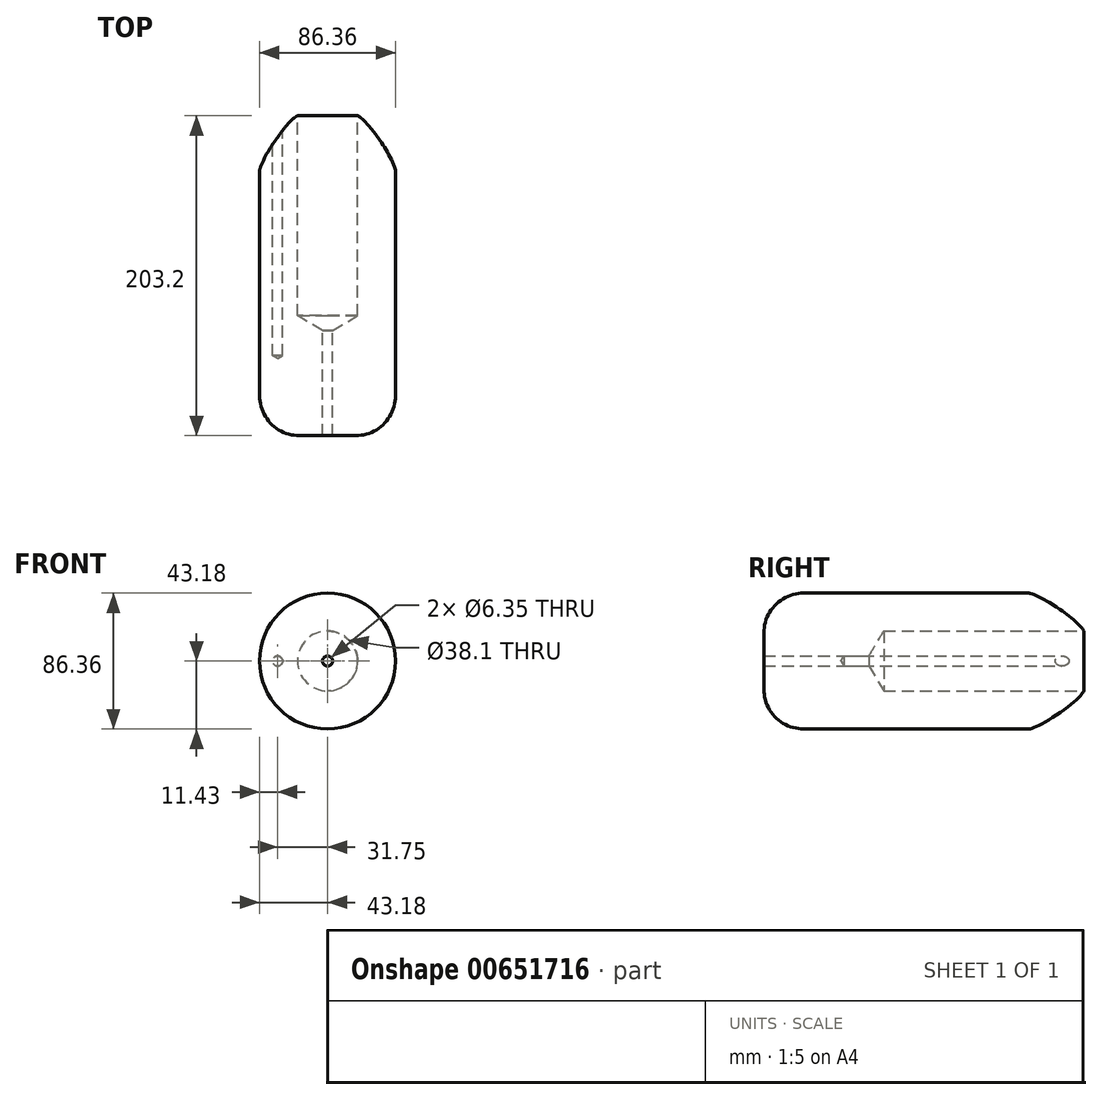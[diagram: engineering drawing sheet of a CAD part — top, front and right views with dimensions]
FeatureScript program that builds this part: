
annotation { "Feature Type Name" : "Feature", "Feature Type Description" : "" }
export const myFeature = defineFeature(function(context is Context, id is Id, definition is map)
    precondition{}
    {
        {
            var Q0;
            Q0=qCreatedBy(makeId("Front.planeOp"),FACE);
            var sketch = newSketch(context, id + "F0", { "sketchPlane" : qUnion([Q0])});
            skCircle(sketch, "E0", {"center": v(0, 0) * mm, "radius": 43.18 * mm});
            skSolve(sketch);
        }
        {
            var Q0;
            Q0=qCreatedBy(makeId("Front.planeOp"),FACE);
            var sketch = newSketch(context, id + "F1", { "sketchPlane" : qUnion([Q0])});
            skCircle(sketch, "E1", {"center": v(0, 0) * mm, "radius": 19.05 * mm});
            skSolve(sketch);
        }
        {
            var Q0;
            Q0=qCreatedBy(makeId("Front.planeOp"),FACE);
            var sketch = newSketch(context, id + "F2", { "sketchPlane" : qUnion([Q0])});
            skCircle(sketch, "E2", {"center": v(0, 0) * mm, "radius": 31.75 * mm});
            skCircle(sketch, "E3", {"center": v(0, -31.75) * mm, "radius": 3.18 * mm});
            skCircle(sketch, "E4", {"center": v(-31.75, 0) * mm, "radius": 3.18 * mm});
            skCircle(sketch, "E5", {"center": v(0, 31.75) * mm, "radius": 3.18 * mm});
            skCircle(sketch, "E6", {"center": v(31.75, 0) * mm, "radius": 3.18 * mm});
            skCircle(sketch, "E7", {"center": v(0, 0) * mm, "radius": 25.4 * mm});
            skCircle(sketch, "E8", {"center": v(25.4, 0) * mm, "radius": 3.18 * mm});
            skSolve(sketch);
        }
        {
            var Q0;
            Q0=makeQuery(id+"F0.imprint","IMPRINT",FACE,{"disambiguationData":[TD([[makeQuery(id+"F0.imprint","IMPRINT",EDGE,{"derivedFrom":sQuery(id+"F0.wireOp",EDGE,"E0")}),1.0]])]});
            extrude(context, id + "F3", {"entities" : qUnion([Q0]), "depth" : 203.2 * mm, "offsetDistance" : 25.4 * mm});
        }
        {
            var Q0;
            Q0=sQuery(id+"F1.wireOp",VERTEX,"E1.center");
            var Q1;
            Q1=makeQuery(id+"F3.opExtrude","SWEPT_BODY",BODY,{"disambiguationData":[OSD([sQuery(id+"F0.wireOp",EDGE,"E0")])]});
            hole(context, id + "F4", {"style" : HoleStyle.SIMPLE, "endStyle" : HoleEndStyle.BLIND, "oppositeDirection" : true, "holeDiameter" : 38.1 * mm, "majorDiameter" : 6.35 * mm, "holeDepth" : 127 * mm, "isTappedThrough" : true, "tappedDepth" : 12.7 * mm, "tapClearance" : 3, "locations" : qUnion([Q0]), "scope" : qUnion([Q1])});
        }
        {
            var Q0;
            Q0=sQuery(id+"F1.wireOp",VERTEX,"E1.center");
            var Q1;
            Q1=makeQuery(id+"F3.opExtrude","SWEPT_BODY",BODY,{"disambiguationData":[OSD([sQuery(id+"F0.wireOp",EDGE,"E0")])]});
            hole(context, id + "F5", {"style" : HoleStyle.SIMPLE, "endStyle" : HoleEndStyle.THROUGH, "oppositeDirection" : true, "holeDiameter" : 6.35 * mm, "majorDiameter" : 6.35 * mm, "isTappedThrough" : true, "tappedDepth" : 12.7 * mm, "tapClearance" : 3, "locations" : qUnion([Q0]), "scope" : qUnion([Q1])});
        }
        {
            var Q0;
            Q0=makeQuery(id+"F3.opExtrude","CAP_EDGE",EDGE,{"disambiguationData":[OSD([sQuery(id+"F0.wireOp",EDGE,"E0")])],"isStart":false});
            fillet(context, id + "F6", {"entities" : qUnion([Q0]), "radius" : 25.4 * mm, "tangentPropagation" : true, "allowEdgeOverflow" : false});
        }
        {
            var Q0;
            Q0=sQuery(id+"F2.wireOp",VERTEX,"E4.center");
            var Q1;
            Q1=makeQuery(id+"F3.opExtrude","SWEPT_BODY",BODY,{"disambiguationData":[OSD([sQuery(id+"F0.wireOp",EDGE,"E0")])]});
            hole(context, id + "F7", {"style" : HoleStyle.SIMPLE, "endStyle" : HoleEndStyle.BLIND, "oppositeDirection" : true, "holeDiameter" : 6.35 * mm, "majorDiameter" : 6.35 * mm, "holeDepth" : 152.4 * mm, "isTappedThrough" : true, "tappedDepth" : 12.7 * mm, "tapClearance" : 3, "locations" : qUnion([Q0]), "scope" : qUnion([Q1])});
        }
        {
            var Q0;
            Q0=makeQuery(id+"F3.opExtrude","CAP_EDGE",EDGE,{"disambiguationData":[OSD([sQuery(id+"F0.wireOp",EDGE,"E0")])],"isStart":true});
            fillet(context, id + "F8", {"entities" : qUnion([Q0]), "radius" : 38.1 * mm, "tangentPropagation" : true, "rho" : 0.2, "crossSection" : FilletCrossSection.CONIC, "allowEdgeOverflow" : false});
        }
    });
